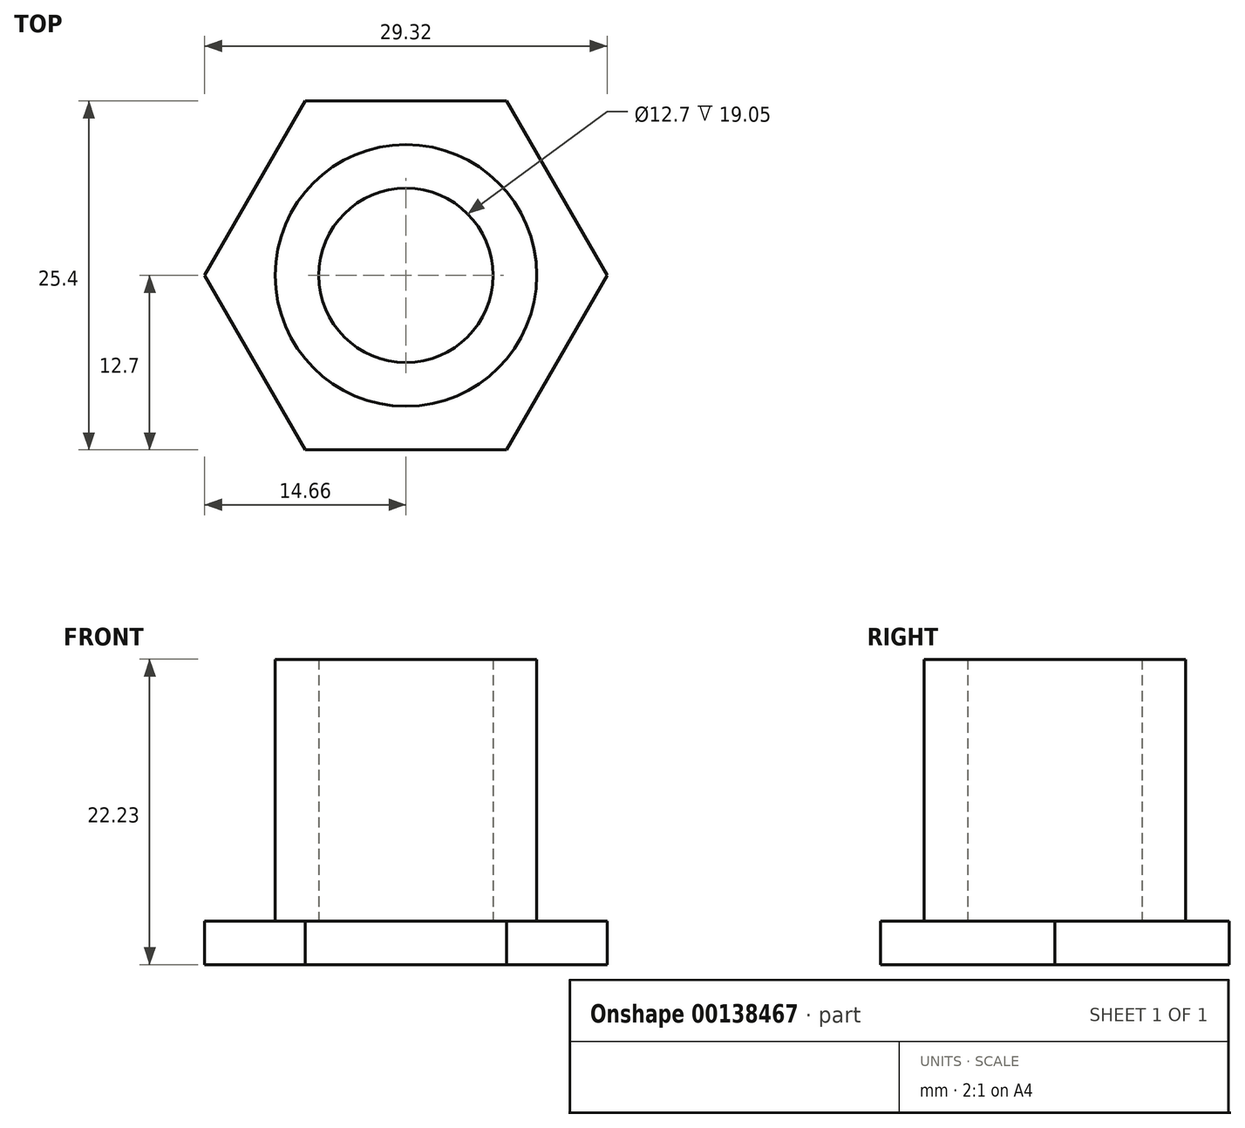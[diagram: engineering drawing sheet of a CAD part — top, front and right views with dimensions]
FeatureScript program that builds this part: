
annotation { "Feature Type Name" : "Feature", "Feature Type Description" : "" }
export const myFeature = defineFeature(function(context is Context, id is Id, definition is map)
    precondition{}
    {
        {
            var Q0;
            Q0=qCreatedBy(makeId("Top.planeOp"),FACE);
            var sketch = newSketch(context, id + "F0", { "sketchPlane" : qUnion([Q0])});
            skCircle(sketch, "E0.cCircle", {"center": v(0, 0) * mm, "radius": 12.7 * mm, "construction": true});
            skLineSegment(sketch, "E0.0", {"start": v(7.33, -12.7) * mm, "end": v(-7.33, -12.7) * mm});
            skLineSegment(sketch, "E0.1", {"start": v(-7.33, -12.7) * mm, "end": v(-14.66, 0) * mm});
            skLineSegment(sketch, "E0.2", {"start": v(-14.66, 0) * mm, "end": v(-7.33, 12.7) * mm});
            skLineSegment(sketch, "E0.3", {"start": v(-7.33, 12.7) * mm, "end": v(7.33, 12.7) * mm});
            skLineSegment(sketch, "E0.4", {"start": v(7.33, 12.7) * mm, "end": v(14.66, 0) * mm});
            skLineSegment(sketch, "E0.5", {"start": v(14.66, 0) * mm, "end": v(7.33, -12.7) * mm});
            skPoint(sketch, "E0.0.midPoint", {"position": v(0, -12.7) * mm});
            skSolve(sketch);
        }
        {
            var Q0;
            Q0 = qSketchRegion(id + "F0", true);
            extrude(context, id + "F1", {"entities" : qUnion([Q0]), "depth" : 3.17 * mm});
        }
        {
            var Q0;
            Q0=makeQuery(id+"F1.opExtrude","CAP_FACE",FACE,{"disambiguationData":[OSD([sQuery(id+"F0.wireOp",EDGE,"E0.0"),sQuery(id+"F0.wireOp",EDGE,"E0.1"),sQuery(id+"F0.wireOp",EDGE,"E0.2"),sQuery(id+"F0.wireOp",EDGE,"E0.3"),sQuery(id+"F0.wireOp",EDGE,"E0.4"),sQuery(id+"F0.wireOp",EDGE,"E0.5")])],"isStart":false});
            var sketch = newSketch(context, id + "F2", { "sketchPlane" : qUnion([Q0])});
            skCircle(sketch, "E1", {"center": v(0, 0) * mm, "radius": 9.53 * mm});
            skCircle(sketch, "E2", {"center": v(0, 0) * mm, "radius": 6.35 * mm});
            skSolve(sketch);
        }
        {
            var Q0;
            Q0 = qSketchRegion(id + "F2", true);
            extrude(context, id + "F3", {"entities" : qUnion([Q0]), "operationType" : NewBodyOperationType.ADD, "depth" : 19.05 * mm});
        }
    });
